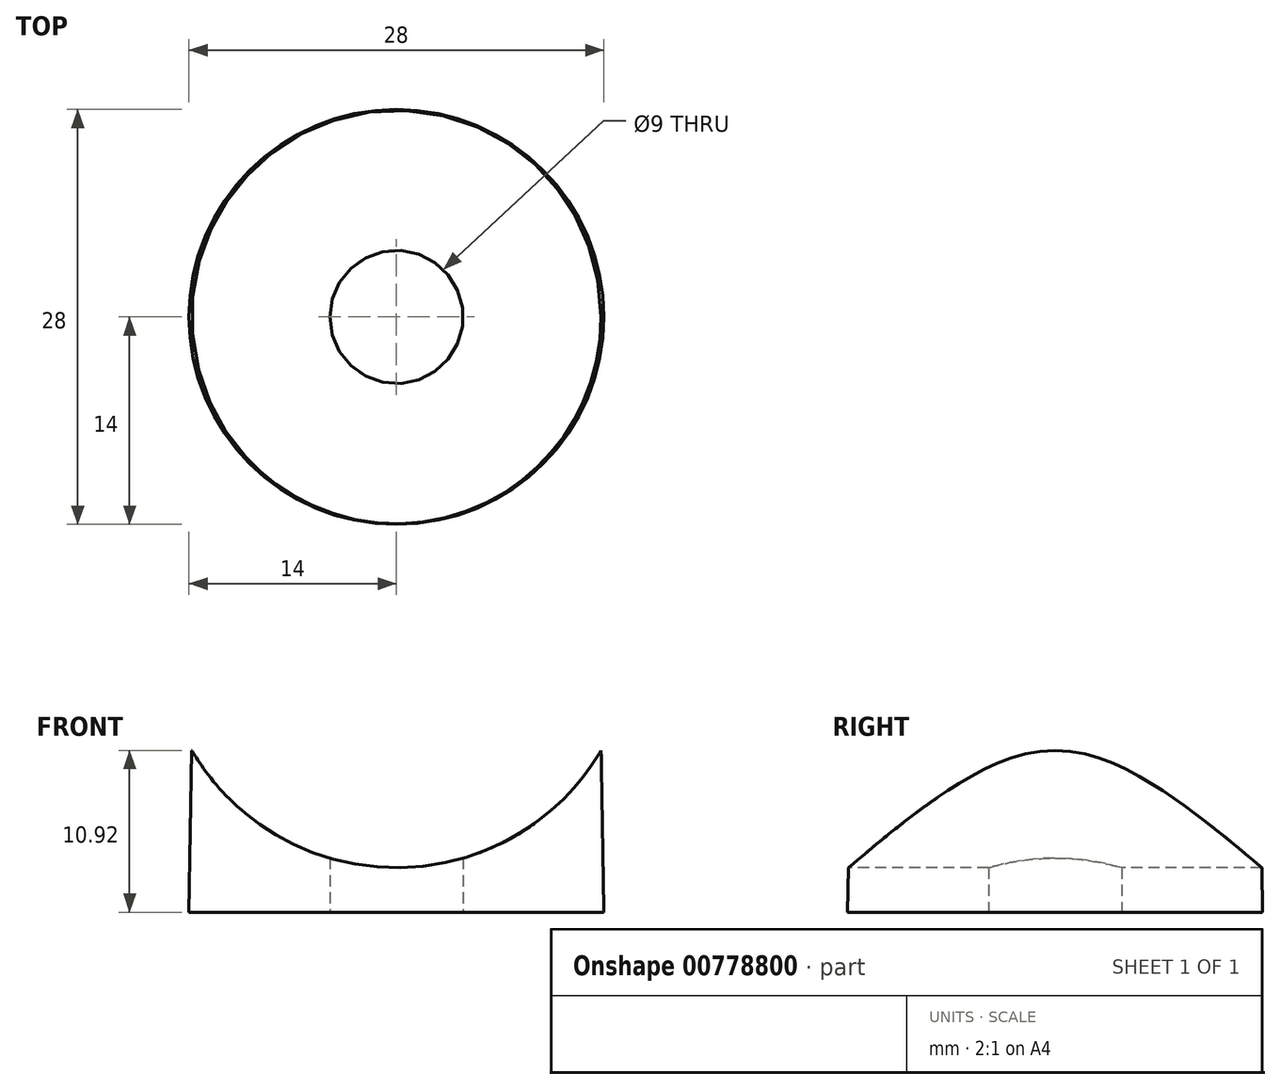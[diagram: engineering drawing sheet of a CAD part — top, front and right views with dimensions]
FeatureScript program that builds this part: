
annotation { "Feature Type Name" : "Feature", "Feature Type Description" : "" }
export const myFeature = defineFeature(function(context is Context, id is Id, definition is map)
    precondition{}
    {
        {
            var Q0;
            Q0=qCreatedBy(makeId("Top.planeOp"),FACE);
            var sketch = newSketch(context, id + "F0", { "sketchPlane" : qUnion([Q0])});
            skCircle(sketch, "E0", {"center": v(0, 0) * mm, "radius": 14 * mm});
            skSolve(sketch);
        }
        {
            var Q0;
            Q0 = qSketchRegion(id + "F0", true);
            extrude(context, id + "F1", {"entities" : qUnion([Q0]), "depth" : 12 * mm, "offsetDistance" : 25 * mm, "hasDraft" : true, "draftAngle" : 1 * degree, "draftPullDirection" : true});
        }
        {
            var Q0;
            Q0=qCreatedBy(makeId("Front.planeOp"),FACE);
            var sketch = newSketch(context, id + "F2", { "sketchPlane" : qUnion([Q0])});
            skCircle(sketch, "E1", {"center": v(0, 19) * mm, "radius": 16 * mm});
            skSolve(sketch);
        }
        {
            var Q0;
            Q0 = qSketchRegion(id + "F2", true);
            extrude(context, id + "F3", {"entities" : qUnion([Q0]), "operationType" : NewBodyOperationType.REMOVE, "oppositeDirection" : true, "depth" : 32 * mm, "offsetDistance" : 25 * mm, "symmetric" : true});
        }
        {
            var Q0;
            Q0=makeQuery(id+"F1.opExtrude","CAP_FACE",FACE,{"disambiguationData":[OSD([sQuery(id+"F0.wireOp",EDGE,"E0")])],"isStart":true});
            var sketch = newSketch(context, id + "F4", { "sketchPlane" : qUnion([Q0])});
            skCircle(sketch, "E2", {"center": v(0, 0) * mm, "radius": 4.5 * mm});
            skSolve(sketch);
        }
        {
            var Q0;
            Q0 = qSketchRegion(id + "F4", true);
            extrude(context, id + "F5", {"entities" : qUnion([Q0]), "operationType" : NewBodyOperationType.REMOVE, "oppositeDirection" : true, "depth" : 5 * mm, "offsetDistance" : 25 * mm});
        }
    });
